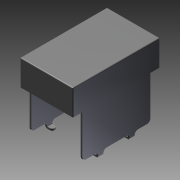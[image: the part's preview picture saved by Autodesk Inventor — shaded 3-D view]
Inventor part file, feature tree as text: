
AUTODESK INVENTOR PART (.ipt)
format: ipt  version: 2015 (Build 190159000, 159)  size: 217,600 bytes
history: native  units: in
note: dims shown in document units (in); Inventor stores cm internally (conversion verified against a paired STEP export)
features: other x14, extrude x10, sketch x10
ambient origin geometry x8: Origin, YZ Plane, XZ Plane, XY Plane, X Axis, Y Axis, Z Axis, Center Point
bodies: Solid1 (feature_tree)
feature tree (34):
  extrude  "Extrusion1"  Depth=0.01in TaperAngle=0.0deg
  extrude  "Extrusion2"  Depth=0.6in TaperAngle=0.0deg
  extrude  "Extrusion3"  Depth=0.405in TaperAngle=0.0deg
  extrude  "Extrusion4"  Depth=0.01in TaperAngle=0.0deg
  extrude  "Extrusion5"  Depth=0.01in TaperAngle=0.0deg
  extrude  "Extrusion6"  [1 undecoded]
  extrude  "Extrusion7"  [1 undecoded]
  extrude  "Extrusion8"  [1 undecoded]
  extrude  "Extrusion9"  [1 undecoded]
  extrude  "Extrusion10"  [1 undecoded]
  other  "to_body_XY"
  other  "to_body_YZ"
  other  "to_body_ZX"
  other  "to_body_X"
  other  "to_body_Y"
  other  "to_body_Z"
  other  "to_body_Center"
  other  "to_bushings_XY"
  other  "to_bushings_YZ"
  other  "to_bushings_ZX"
  other  "to_bushings_X"
  other  "to_bushings_Y"
  other  "to_bushings_Z"
  other  "to_bushings_Center"
  sketch  "Sketch_1"  dims[d0=0.141in d1=0.0in d2=0.01in d3=0.0in]
  sketch  "Sketch_2"  dims[d4=0.6in d5=0.0in d6=0.6in d7=0.0in]
  sketch  "Sketch_7"  dims[d8=0.311in d9=0.0in d10=0.405in d11=0.0in]
  sketch  "Sketch_8"  dims[d12=0.01in d13=0.0in d14=0.01in d15=0.0in]
  sketch  "Sketch_13"  dims[d16=0.01in d17=0.0in d18=0.01in d19=0.0in]
  sketch  "Sketch_14"
  sketch  "Sketch_29"
  sketch  "Sketch_30"
  sketch  "Sketch_31"
  sketch  "Sketch_32"
note: 5 required parameter values undecoded (feature->parameter linkage not recoverable at this tier; creation-order binding heuristic only, values carry confidence <= 0.55)
